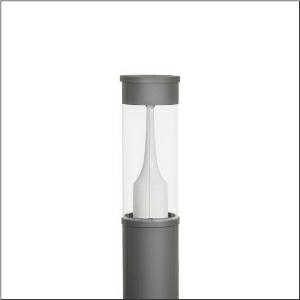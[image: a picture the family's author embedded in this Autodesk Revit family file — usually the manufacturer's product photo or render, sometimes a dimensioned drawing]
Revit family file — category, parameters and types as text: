
# Revit family: city-light_120_iq___pl1_2s_5xa5285of14h_ee05
name_source: partatom
category: Lighting Fixtures
units: mm (PartAtom-declared; Revit-internal decimal feet)

## family parameters
Cut with Voids When Loaded = No
Host = Face
Light Source = No
Part Type = Normal
Room Calculation Point = No
Round Connector Dimension = Use Diameter
Shared = No

## types (1)
- --- (1 x LED, 2970 lm, 21.8 W, 2700K)
    Apparent Load = 22 VA
    CIE Flux Codes = 23 62 94 96 100
    Color Rendering = 70
    Color Temperature = 2700K
    Default Elevation = 1800 mm
    Description = City-Light 120 iQ, bollard luminaire, Module 540 iQ-SR, primary light control with 3 zone facetted reflector, of plastic, silver coated, highly specular, structured, primary optical cover: cover, of PMMA, transparent, partly coated, light distribution: PL1.2s, primary light characteristic: symmetric, LED, High Power LED, rated luminous flux: 2.970lm, luminous efficacy: 136lm/W, light colour: 727, colour temperature: 2700K, control gear: iQ Street-Remote, control: pre-setting: logarithmic dimming characteristic, Street-Remote, Auto-Match, Temp-Guard, Lumen-Switch, Night-Set, Smart-Wire, Light-Fading, Desk-Remote (wireless, voltage-free reading and setting of iQ features in the workshop via application-optimized NFC function/RFID function), optimised constant luminous flux control (CLO 2.0), with terminal, 6-pole, max. 2.5mm², mains connection: 230..240V, AC, 50/60Hz, start of lifetime: 22W, end of service life: 23W, reduction: 11W, luminaire housing, cylindrical, of extruded aluminium section, coated, Siteco® metallic grey (DB 702S), length: 1.200mm, diameter: 200mm, Module 540 iQ-SR, traffic white (RAL 9016), equipment: standard, protection rating (complete): IP54, insulation class (complete): insulation class II (safety insulation), certification: CE, ENEC, VDE, packaging unit: 1 piece

Light Distribution: PL1.2s
    Height = 500 mm
    Lamp = 1 x LED
    Lamp Light Flux = 2970 lm
    Lamp Power = 21.8 W
    Lamp count = 1
    Length = 200 mm  [stored 0.656168 ft]
    Luminous efficacy = 136 lm/W
    Manufacturer = Siteco
    ModVariant = No
    Model = 5XA5285OF14H
    Mounting Place = Floor
    Mounting Type = Freestanding
    Number of Poles = 1
    OnlyDefault = Yes
    Power Factor = 1
    Product Name = City-Light 120 iQ | PL1.2s
    Product group = bollard luminaire
    ProductGroupID = 1304
    Protection Class = Protection class II
    Protection Degree = IP 54
    RLX_Detail_Level = 1
    RLX_Emergency_Light_Flux = 0 lm
    RLX_Emergency_Type = 0
    RLX_Emergency_Type_DB = No
    RlxData = <blob elided: 30249 chars, md5=a6589364>
    Socket = socket
    Standby Power = 0 W
    System Light Flux = 2970 lm
    System Power = 22 W
    Type Comments = factory setting: luminous flux: 100 % | dim-lin: 254 | 456 mA
    Type Image = l_1006922.jpg
    URL = http://relux.com
    VarID = @adj_144617
    Voltage = 0 V
    Weight = 0.00 kg
    Width = 0 mm  [stored 0 ft]

note: [stored X ft] marks values corroborated as IEEE doubles in the binary element streams (Revit-internal decimal feet)

## geometry (parser evidence)
native form markers: Blend x4, Sweep x10
no freeform markers — native parametric forms only
